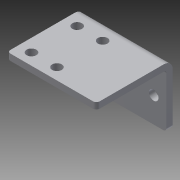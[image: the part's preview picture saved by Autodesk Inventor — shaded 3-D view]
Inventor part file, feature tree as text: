
AUTODESK INVENTOR PART (.ipt)
format: ipt  version: 2014 (Build 180170000, 170)  size: 189,952 bytes
history: native  units: in
note: dims shown in document units (in); Inventor stores cm internally (conversion verified against a paired STEP export)
features: sheet_metal_op x4, other x4, sketch x3, fillet x1, extrude x1
ambient origin geometry x8: Origin, YZ Plane, XZ Plane, XY Plane, X Axis, Y Axis, Z Axis, Center Point
bodies: Solid1 (feature_tree)
feature tree (13):
  sheet_metal_op  "Face1"
  sheet_metal_op  "Flange1"
  fillet  "Fillet1"  Radius=1.75in
  extrude  "Extrusion1"  Depth=0.19in
  sketch  "Sketch1"  dims[d1=1.0in d2=0.19in]
  other  "Plate1"
  sketch  "Sketch2"  dims[d4=0.7874in d6=1.0in d7=0.3937in d9=1.0in]
  other  "Plate2"
  sheet_metal_op  "Bend1"
  sheet_metal_op  "Corner1"
  sketch  "Sketch3"  dims[d11=0.125in d12=0.125in d13=0.0625in d14=0.25in d15=0.125in d16=1.5in d17=90.0deg d18=0.05in d19=0.5in d20=0.125in d21=0.125in d22=0.0625in d23=1.35in d24=0.75in d27=0.19in d28=0.125in d29=0.2265in d30=1.0in d31=0.0in d32=0.25in d33=0.875in d3=0.0in]
  other  "Definition1"
  other  "Cut1"
